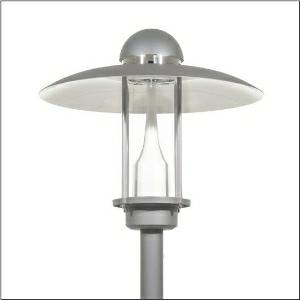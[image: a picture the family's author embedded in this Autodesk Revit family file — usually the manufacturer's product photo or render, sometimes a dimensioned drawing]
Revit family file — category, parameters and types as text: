
# Revit family: city-light_elegance_iq___pl1_2s_5xa5265cf14h_c70b
name_source: partatom
category: Lighting Fixtures
units: mm (PartAtom-declared; Revit-internal decimal feet)

## family parameters
Cut with Voids When Loaded = No
Host = Face
Light Source = No
Part Type = Normal
Room Calculation Point = No
Round Connector Dimension = Use Diameter
Shared = No

## types (1)
- --- (1 x LED, 2840 lm, 23.9 W, 2200K)
    Apparent Load = 24 VA
    CIE Flux Codes = 24 63 94 98 100
    Color Rendering = 70
    Color Temperature = 2200K
    Default Elevation = 1800 mm
    Description = City-Light Elegance iQ, mast luminaire, Module 540 iQ-SR, primary light control with 3 zone facetted reflector, of plastic, silver coated, highly specular, structured, primary optical cover: cover, of PMMA, transparent, light distribution: PL1.2s, light emission: direct distribution, primary light characteristic: symmetric, installation type: post-top, LED, High Power LED, rated luminous flux: 2.840lm, luminous efficacy: 119lm/W, light colour: 722, colour temperature: 2200K, control gear: iQ Street-Remote, control: pre-setting: logarithmic dimming characteristic, Street-Remote, Auto-Match, Temp-Guard, Lumen-Switch, Night-Set, Smart-Wire, Light-Fading, Desk-Remote (wireless, voltage-free reading and setting of iQ features in the workshop via application-optimized NFC function/RFID function), optimised constant luminous flux control (CLO 2.0), with terminal, 6-pole, max. 2.5mm², mains connection: 230..240V, AC, 50/60Hz, start of lifetime: 24W, end of service life: 26W, reduction: 12W, luminaire housing, upper part, of aluminium, coated, Siteco® metallic grey (DB 702S), diameter: 750mm, height: 675mm, spigot size: d x l = 76 x 70mm (post-top) | with reducer (optional accessory) 60 x 70mm, mounting height: 3..5m, post-top mast mounting element, of diecast aluminium, coated, Siteco® metallic grey (DB 702S), Module 540 iQ-SR, traffic white (RAL 9016), equipment: standard, protection rating (complete): IP65, insulation class (complete): insulation class II (safety insulation), certification: CE, ENEC, VDE, packaging unit: 1 piece

Light Distribution: PL1.2s
    Height = 675 mm
    Lamp = 1 x LED
    Lamp Light Flux = 2840 lm
    Lamp Power = 23.9 W
    Lamp count = 1
    Length = 750 mm
    Luminous efficacy = 119 lm/W
    Manufacturer = Siteco
    ModVariant = No
    Model = 5XA5265CF14H
    Number of Poles = 1
    OnlyDefault = Yes
    Power Factor = 1
    Product Name = City-Light Elegance iQ | PL1.2s
    Product group = mast luminaire | pylon top
    ProductGroupID = 6100
    Protection Class = Protection class II
    Protection Degree = IP 65
    RLX_Detail_Level = 1
    RLX_Emergency_Light_Flux = 0 lm
    RLX_Emergency_Type = 0
    RLX_Emergency_Type_DB = No
    RlxData = <blob elided: 33697 chars, md5=389bc08d>
    Socket = socket
    Standby Power = 0 W
    System Light Flux = 2840 lm
    System Power = 24 W
    Type Comments = factory setting: luminous flux: 100 % | dim-lin: 254 | 499 mA
    Type Image = l_1006912.jpg
    URL = http://relux.com
    VarID = @adj_166891
    Voltage = 0 V
    Weight = 0.00 kg
    Width = 0 mm  [stored 0 ft]

note: [stored X ft] marks values corroborated as IEEE doubles in the binary element streams (Revit-internal decimal feet)

## geometry (parser evidence)
native form markers: Blend x4, Sweep x10
no freeform markers — native parametric forms only
